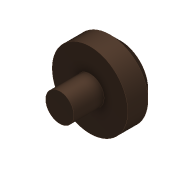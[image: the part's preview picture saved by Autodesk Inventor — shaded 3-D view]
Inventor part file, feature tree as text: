
AUTODESK INVENTOR PART (.ipt)
format: ipt  version: 2017 (Build 210142000, 142)  size: 98,304 bytes
history: native  units: mm
features: revolve x1, sketch x1
ambient origin geometry x8: Origin, YZ Plane, XZ Plane, XY Plane, X Axis, Y Axis, Z Axis, Center Point
bodies: Solid1 (feature_tree)
feature tree (2):
  revolve  "Revolution1"  [1 undecoded]
  sketch  "Sketch1"  dims[d10=90.0deg]
note: 1 required parameter value undecoded (feature->parameter linkage not recoverable at this tier; creation-order binding heuristic only, values carry confidence <= 0.55)
